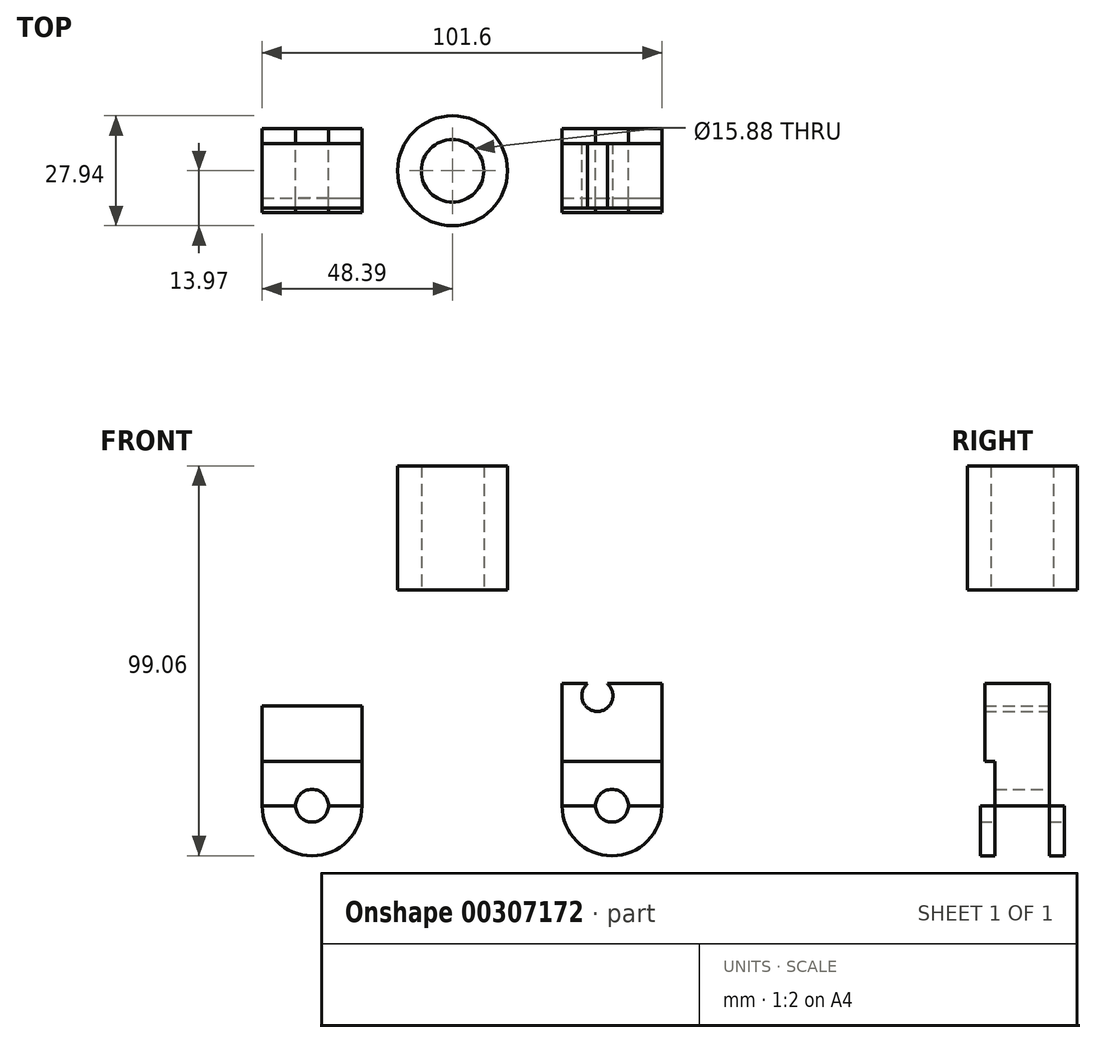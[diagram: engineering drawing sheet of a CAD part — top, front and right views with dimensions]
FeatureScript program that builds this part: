
annotation { "Feature Type Name" : "Feature", "Feature Type Description" : "" }
export const myFeature = defineFeature(function(context is Context, id is Id, definition is map)
    precondition{}
    {
        {
            var Q0;
            Q0=qCreatedBy(makeId("Front.planeOp"),FACE);
            var sketch = newSketch(context, id + "F0", { "sketchPlane" : qUnion([Q0])});
            skCircle(sketch, "E0", {"center": v(40.5, 0) * mm, "radius": 12.7 * mm});
            skLineSegment(sketch, "E1", {"start": v(-35.7, 0) * mm, "end": v(40.5, 0) * mm});
            skCircle(sketch, "E2", {"center": v(-35.7, 0) * mm, "radius": 4.17 * mm});
            skCircle(sketch, "E3", {"center": v(40.5, 0) * mm, "radius": 4.17 * mm});
            skCircle(sketch, "E4", {"center": v(-35.7, 0) * mm, "radius": 12.7 * mm});
            skLineSegment(sketch, "E5", {"start": v(53.2, 0) * mm, "end": v(53.2, 47.8) * mm});
            skCircle(sketch, "E6", {"center": v(36.8, 27.94) * mm, "radius": 0.16 * mm});
            skCircle(sketch, "E7", {"center": v(36.8, 27.94) * mm, "radius": 3.96 * mm});
            skLineSegment(sketch, "E8", {"start": v(-48.4, 0) * mm, "end": v(-48.4, 25.4) * mm});
            skLineSegment(sketch, "E9", {"start": v(-23, 0) * mm, "end": v(-23, 45.72) * mm});
            skLineSegment(sketch, "E10", {"start": v(27.8, 0) * mm, "end": v(27.8, 47.8) * mm});
            skLineSegment(sketch, "E11", {"start": v(-48.4, 25.4) * mm, "end": v(-23, 25.4) * mm});
            skPoint(sketch, "E12.orphan", {"position": v(53.2, 45.72) * mm});
            skLineSegment(sketch, "E13", {"start": v(27.8, 47.8) * mm, "end": v(53.2, 47.8) * mm});
            skLineSegment(sketch, "E14", {"start": v(0, 0) * mm, "end": v(0, 86.36) * mm, "construction": true});
            skLineSegment(sketch, "E15.bottom", {"start": v(7.94, 86.36) * mm, "end": v(13.97, 86.36) * mm});
            skLineSegment(sketch, "E15.top", {"start": v(7.94, 54.86) * mm, "end": v(13.97, 54.86) * mm});
            skLineSegment(sketch, "E15.left", {"start": v(7.94, 86.36) * mm, "end": v(7.94, 54.86) * mm});
            skLineSegment(sketch, "E15.right", {"start": v(13.97, 86.36) * mm, "end": v(13.97, 54.86) * mm});
            skSolve(sketch);
        }
        {
            var Q0;
            Q0=makeQuery(id+"F0.imprint","IMPRINT",FACE,{"disambiguationData":[TD([[makeQuery(id+"F0.imprint","IMPRINT",EDGE,{"derivedFrom":sQuery(id+"F0.wireOp",EDGE,"E15.bottom")}),-1.0]])]});
            var Q1;
            Q1=sQuery(id+"F0.wireOp",EDGE,"E14");
            revolve(context, id + "F1", {"entities" : qUnion([Q0]), "axis" : qUnion([Q1]), "revolveType" : RevolveType.FULL});
        }
        {
            var Q0;
            {var subQ0=sQuery(id+"F0.wireOp",EDGE,"E8");Q0=makeQuery(id+"F0.imprint","IMPRINT",FACE,{"disambiguationData":[TD([[makeQuery(id+"F0.imprint","IMPRINT",EDGE,{"derivedFrom":subQ0}),-1.0]])]});}
            var Q1;
            Q1=makeQuery(id+"F0.imprint","IMPRINT",FACE,{"disambiguationData":[TD([[makeQuery(id+"F0.imprint","IMPRINT",EDGE,{"derivedFrom":sQuery(id+"F0.wireOp",EDGE,"E2")}),-1.0]])]});
            var Q2;
            {var subQ1=sQuery(id+"F0.wireOp",EDGE,"E5");Q2=makeQuery(id+"F0.imprint","IMPRINT",FACE,{"disambiguationData":[TD([[makeQuery(id+"F0.imprint","IMPRINT",EDGE,{"derivedFrom":subQ1}),1.0]])]});}
            var Q3;
            Q3=makeQuery(id+"F0.imprint","IMPRINT",FACE,{"disambiguationData":[TD([[makeQuery(id+"F0.imprint","IMPRINT",EDGE,{"derivedFrom":sQuery(id+"F0.wireOp",EDGE,"E3")}),-1.0]])]});
            extrude(context, id + "F2", {"entities" : qUnion([Q0, Q1, Q2, Q3]), "operationType" : NewBodyOperationType.ADD, "endBound" : BoundingType.SYMMETRIC, "depth" : 21.34 * mm});
        }
        {
            var Q0;
            Q0=makeQuery(id+"F2.opExtrude","SWEPT_FACE",FACE,{"disambiguationData":[OSD([sQuery(id+"F0.wireOp",EDGE,"E5")])]});
            var sketch = newSketch(context, id + "F3", { "sketchPlane" : qUnion([Q0])});
            skLineSegment(sketch, "E16.top", {"start": v(6.96, -16.69) * mm, "end": v(-6.96, -16.69) * mm});
            skLineSegment(sketch, "E16.left", {"start": v(6.96, 31.01) * mm, "end": v(6.96, -16.69) * mm});
            skLineSegment(sketch, "E16.right", {"start": v(-6.96, 31.01) * mm, "end": v(-6.96, -16.69) * mm});
            skPoint(sketch, "E16.middle", {"position": v(0, 15.56) * mm});
            skPoint(sketch, "E17.oppositeSnap0", {"position": v(6.96, 15.56) * mm});
            skLineSegment(sketch, "E17.bottom", {"start": v(-6.96, -16.69) * mm, "end": v(6.96, -16.69) * mm});
            skLineSegment(sketch, "E17.top", {"start": v(-6.96, 11.25) * mm, "end": v(6.96, 11.25) * mm});
            skLineSegment(sketch, "E17.left", {"start": v(-6.96, 11.25) * mm, "end": v(-6.96, -16.69) * mm});
            skLineSegment(sketch, "E17.right", {"start": v(6.96, 11.25) * mm, "end": v(6.96, -16.69) * mm});
            skLineSegment(sketch, "E18.bottom", {"start": v(6.96, 31.01) * mm, "end": v(-9.52, 31.01) * mm});
            skLineSegment(sketch, "E18.top", {"start": v(6.96, 11.25) * mm, "end": v(-9.52, 11.25) * mm});
            skLineSegment(sketch, "E18.left", {"start": v(6.96, 31.01) * mm, "end": v(6.96, 11.25) * mm});
            skLineSegment(sketch, "E18.right", {"start": v(-9.52, 31.01) * mm, "end": v(-9.52, 11.25) * mm});
            skLineSegment(sketch, "E19.bottom", {"start": v(-4.4, 11.25) * mm, "end": v(10.26, 11.25) * mm});
            skPoint(sketch, "E16.bottom.end.orphan", {"position": v(-6.96, 47.8) * mm});
            skPoint(sketch, "E20.orphan", {"position": v(6.96, 47.8) * mm});
            skLineSegment(sketch, "E21", {"start": v(-6.96, 31.01) * mm, "end": v(-6.96, 45.72) * mm});
            skLineSegment(sketch, "E22", {"start": v(-6.96, 45.72) * mm, "end": v(7.34, 45.72) * mm});
            skLineSegment(sketch, "E23", {"start": v(7.34, 45.72) * mm, "end": v(6.96, 31.01) * mm});
            skSolve(sketch);
        }
        {
            var Q0;
            {var subQ0=sQuery(id+"F3.wireOp",EDGE,"E21");Q0=makeQuery(id+"F3.imprint","IMPRINT",FACE,{"disambiguationData":[TD([[makeQuery(id+"F3.imprint","IMPRINT",EDGE,{"derivedFrom":subQ0}),-1.0]])]});}
            var Q1;
            {var subQ1=sQuery(id+"F3.wireOp",EDGE,"E16.right");Q1=makeQuery(id+"F3.imprint","IMPRINT",FACE,{"disambiguationData":[TD([[makeQuery(id+"F3.imprint","IMPRINT",EDGE,{"derivedFrom":subQ1}),1.0]])]});}
            var Q2;
            {var subQ0=sQuery(id+"F3.wireOp",EDGE,"E18.top");var subQ3=sQuery(id+"F3.wireOp",EDGE,"E19.bottom");var subQ4=makeQuery(id+"F3.imprint","INTERSECT",VERTEX,{"derivedFrom":[subQ0,subQ3]});Q2=makeQuery(id+"F3.imprint","IMPRINT",FACE,{"disambiguationData":[TD([[makeQuery(id+"F3.imprint","IMPRINT",EDGE,{"disambiguationData":[TD([[subQ4,-1.0]])],"derivedFrom":subQ0}),1.0]])]});}
            var Q3;
            {var subQ0=sQuery(id+"F3.wireOp",EDGE,"E17.bottom");Q3=makeQuery(id+"F3.imprint","IMPRINT",FACE,{"disambiguationData":[TD([[makeQuery(id+"F3.imprint","IMPRINT",EDGE,{"derivedFrom":subQ0}),1.0]])]});}
            extrude(context, id + "F4", {"entities" : qUnion([Q0, Q1, Q2, Q3]), "operationType" : NewBodyOperationType.REMOVE, "endBound" : BoundingType.THROUGH_ALL, "oppositeDirection" : true, "depth" : 25.4 * mm});
        }
        {
            var Q0;
            {var subQ0=sQuery(id+"F3.wireOp",EDGE,"E17.bottom");Q0=makeQuery(id+"F3.imprint","IMPRINT",FACE,{"disambiguationData":[TD([[makeQuery(id+"F3.imprint","IMPRINT",EDGE,{"derivedFrom":subQ0}),1.0]])]});}
            var Q1;
            {var subQ0=sQuery(id+"F3.wireOp",EDGE,"E18.top");var subQ3=sQuery(id+"F3.wireOp",EDGE,"E19.bottom");var subQ4=makeQuery(id+"F3.imprint","INTERSECT",VERTEX,{"derivedFrom":[subQ0,subQ3]});Q1=makeQuery(id+"F3.imprint","IMPRINT",FACE,{"disambiguationData":[TD([[makeQuery(id+"F3.imprint","IMPRINT",EDGE,{"disambiguationData":[TD([[subQ4,-1.0]])],"derivedFrom":subQ0}),1.0]])]});}
            extrude(context, id + "F5", {"entities" : qUnion([Q0, Q1]), "operationType" : NewBodyOperationType.REMOVE, "endBound" : BoundingType.THROUGH_ALL, "oppositeDirection" : true, "depth" : 25.4 * mm});
        }
        {
            var Q0;
            Q0=qCreatedBy(makeId("Front.planeOp"),FACE);
            var sketch = newSketch(context, id + "F6", { "sketchPlane" : qUnion([Q0])});
            skLineSegment(sketch, "E24", {"start": v(-31, 24.41) * mm, "end": v(-31, 45.2) * mm});
            skLineSegment(sketch, "E25", {"start": v(-31, 45.2) * mm, "end": v(-16.05, 71.46) * mm});
            skLineSegment(sketch, "E26", {"start": v(33.92, 49.21) * mm, "end": v(16.41, 71.46) * mm});
            skArc(sketch, "E27", {"start": v(16.41, 71.46) * mm, "mid": v(0.18, 80.9) * mm, "end": v(-16.05, 71.46) * mm});
            skLineSegment(sketch, "E28", {"start": v(-31, 24.41) * mm, "end": v(-20.79, 24.41) * mm});
            skLineSegment(sketch, "E29", {"start": v(28.45, 46.3) * mm, "end": v(36.47, 49.21) * mm});
            skSolve(sketch);
        }
        {
            var Q0;
            Q0=sQuery(id+"F6.wireOp",EDGE,"E24");
            var Q1;
            Q1=sQuery(id+"F0.wireOp",EDGE,"E9");
            var Q2;
            Q2=sQuery(id+"F6.wireOp",EDGE,"YMZWFOIQ-NF3z-GPLm-lu6o-DS5CTnnlIgq6");
            var Q3;
            Q3=sQuery(id+"F6.wireOp",EDGE,"E25");
            var Q4;
            Q4=sQuery(id+"F6.wireOp",EDGE,"E27");
            var Q5;
            Q5=sQuery(id+"F6.wireOp",EDGE,"1GEhVdYb-QlMI-QwlG-VMQv-8gShVcsYa4In");
            var Q6;
            Q6=sQuery(id+"F6.wireOp",EDGE,"OeShWMv4-InbI-kCcf-f8QK-uEds8XFeOeeN");
            var Q7;
            Q7=sQuery(id+"F6.wireOp",EDGE,"E26");
            extrude(context, id + "F7", {"bodyType" : ToolBodyType.SURFACE, "surfaceEntities" : qUnion([Q0, Q1, Q2, Q3, Q4, Q5, Q6, Q7]), "depth" : 23.88 * mm});
        }
    });
